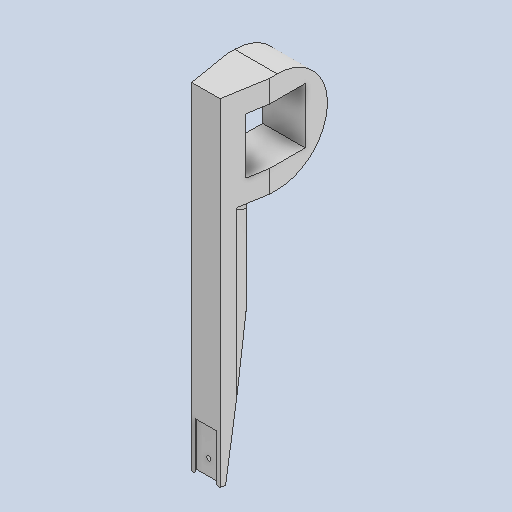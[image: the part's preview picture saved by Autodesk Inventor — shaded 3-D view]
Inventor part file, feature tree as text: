
AUTODESK INVENTOR PART (.ipt)
format: ipt  version: 2023.3 (Build 273359000, 359)  size: 236,544 bytes
history: native  units: mm
features: extrude x5, sketch x5, other x4, chamfer x3, plane x3, fillet x1, reference x1
ambient origin geometry x8: Origin, YZ Plane, XZ Plane, XY Plane, X Axis, Y Axis, Z Axis, Center Point
bodies: Solid1 (feature_tree)
feature tree (22):
  other  "np1_washing_arm"
  extrude  "Extrusion1"  Depth=21.208mm
  extrude  "Extrusion2"  Depth=50.0mm TaperAngle=0.0deg
  extrude  "Extrusion3"  TaperAngle=60.0deg  [1 undecoded]
  chamfer  "Chamfer1"  Distance=10.0mm
  extrude  "Extrusion4"  Depth=1.0mm
  extrude  "Extrusion5"  Depth=5.0mm
  chamfer  "Chamfer2"  Distance=0.64mm
  plane  "Work Plane1"
  plane  "Work Plane2"
  fillet  "Fillet2"  Radius=0.9mm
  plane  "Work Plane3"
  chamfer  "Chamfer3"  Distance=3.5mm
  sketch  "Sketch1"  dims[d0=13.208mm d1=21.208mm]
  sketch  "Sketch2"  dims[d2=9.0mm d3=0.0mm d4=50.0mm d5=0.0mm]
  sketch  "Sketch3"  dims[d7=60.0deg d8=60.0deg d11=10.0mm d12=0.0mm]
  sketch  "Sketch4"  dims[d13=4.0mm d14=30.0mm d15=45.0deg d16=1.0mm]
  sketch  "Sketch5"  dims[d17=1.0mm d18=5.0mm d19=0.64mm d21=0.9mm d22=3.5mm d23=10.0mm d24=0.0mm d25=1.5mm d26=1.5mm d27=0.0mm d33=1.5mm d34=9.0mm d35=45.0deg d47=2.0mm d48=0.2mm d49=2.0mm d50=45.0deg d51=4.523511mm]
  reference  "Reference1"
  parser-record x1  (decoder bookkeeping rows leaked as tree rows — omitted from the tree; the rows remain in map.json)
  other  "washing_assembly.iam"
  other  "wash_ring:1"
note: 1 required parameter value undecoded (feature->parameter linkage not recoverable at this tier; creation-order binding heuristic only, values carry confidence <= 0.55)
note: 1 file-system path scrubbed to <path> (originals preserved in map.json)
